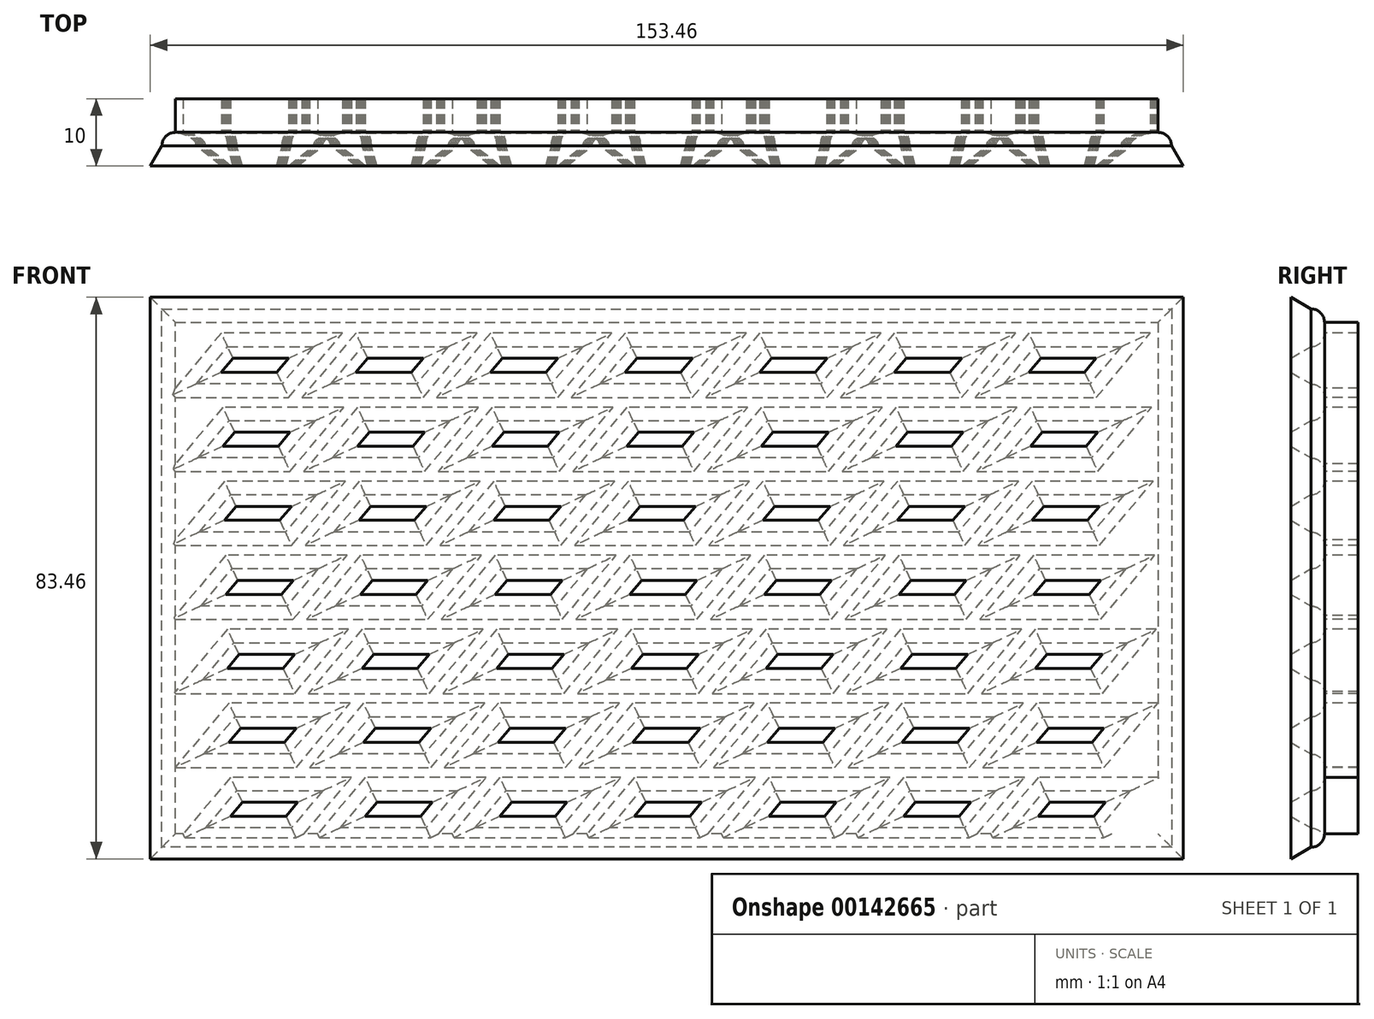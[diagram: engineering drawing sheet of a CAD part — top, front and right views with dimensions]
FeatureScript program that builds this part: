
annotation { "Feature Type Name" : "Feature", "Feature Type Description" : "" }
export const myFeature = defineFeature(function(context is Context, id is Id, definition is map)
    precondition{}
    {
        {
            var Q0;
            Q0=qCreatedBy(makeId("Front.planeOp"),FACE);
            var sketch = newSketch(context, id + "F0", { "sketchPlane" : qUnion([Q0])});
            skLineSegment(sketch, "E0", {"start": v(-73.34, 50) * mm, "end": v(76.66, 50) * mm});
            skLineSegment(sketch, "E1", {"start": v(76.66, 50) * mm, "end": v(76.66, -50) * mm});
            skLineSegment(sketch, "E2", {"start": v(76.66, -50) * mm, "end": v(-73.34, -50) * mm});
            skLineSegment(sketch, "E3", {"start": v(-73.34, -50) * mm, "end": v(-73.34, 50) * mm});
            skLineSegment(sketch, "E4", {"start": v(-73.34, 40) * mm, "end": v(76.66, 40) * mm});
            skLineSegment(sketch, "E5.0", {"start": v(76.66, -40) * mm, "end": v(-73.34, -40) * mm});
            skSolve(sketch);
        }
        {
            var Q0;
            Q0=qCreatedBy(makeId("Front.planeOp"),FACE);
            var sketch = newSketch(context, id + "F1", { "sketchPlane" : qUnion([Q0])});
            skLineSegment(sketch, "E6", {"start": v(-68.22, 28.84) * mm, "end": v(-55.46, 28.84) * mm});
            skLineSegment(sketch, "E7", {"start": v(-55.46, 28.84) * mm, "end": v(-50.8, 34.39) * mm});
            skLineSegment(sketch, "E8", {"start": v(-50.8, 34.39) * mm, "end": v(-63.57, 34.39) * mm});
            skLineSegment(sketch, "E9", {"start": v(-63.57, 34.39) * mm, "end": v(-68.22, 28.84) * mm});
            skLineSegment(sketch, "E10.0.1.0", {"start": v(-50.58, 23.39) * mm, "end": v(-63.34, 23.39) * mm});
            skLineSegment(sketch, "E10.0.1.1", {"start": v(-68, 17.84) * mm, "end": v(-55.24, 17.84) * mm});
            skLineSegment(sketch, "E10.0.1.2", {"start": v(-55.24, 17.84) * mm, "end": v(-50.58, 23.39) * mm});
            skLineSegment(sketch, "E10.0.1.3", {"start": v(-63.34, 23.39) * mm, "end": v(-68, 17.84) * mm});
            skLineSegment(sketch, "E10.0.2.0", {"start": v(-50.35, 12.4) * mm, "end": v(-63.11, 12.4) * mm});
            skLineSegment(sketch, "E10.0.2.1", {"start": v(-67.77, 6.84) * mm, "end": v(-55, 6.84) * mm});
            skLineSegment(sketch, "E10.0.2.2", {"start": v(-55, 6.84) * mm, "end": v(-50.35, 12.4) * mm});
            skLineSegment(sketch, "E10.0.2.3", {"start": v(-63.11, 12.4) * mm, "end": v(-67.77, 6.84) * mm});
            skLineSegment(sketch, "E10.0.3.0", {"start": v(-50.12, 1.4) * mm, "end": v(-62.88, 1.4) * mm});
            skLineSegment(sketch, "E10.0.3.1", {"start": v(-67.54, -4.15) * mm, "end": v(-54.78, -4.15) * mm});
            skLineSegment(sketch, "E10.0.3.2", {"start": v(-54.78, -4.15) * mm, "end": v(-50.12, 1.4) * mm});
            skLineSegment(sketch, "E10.0.3.3", {"start": v(-62.88, 1.4) * mm, "end": v(-67.54, -4.15) * mm});
            skLineSegment(sketch, "E10.0.4.0", {"start": v(-49.9, -9.6) * mm, "end": v(-62.66, -9.6) * mm});
            skLineSegment(sketch, "E10.0.4.1", {"start": v(-67.31, -15.15) * mm, "end": v(-54.55, -15.15) * mm});
            skLineSegment(sketch, "E10.0.4.2", {"start": v(-54.55, -15.15) * mm, "end": v(-49.9, -9.6) * mm});
            skLineSegment(sketch, "E10.0.4.3", {"start": v(-62.66, -9.6) * mm, "end": v(-67.31, -15.15) * mm});
            skLineSegment(sketch, "E10.0.5.0", {"start": v(-49.67, -20.6) * mm, "end": v(-62.43, -20.6) * mm});
            skLineSegment(sketch, "E10.0.5.1", {"start": v(-67.08, -26.15) * mm, "end": v(-54.32, -26.15) * mm});
            skLineSegment(sketch, "E10.0.5.2", {"start": v(-54.32, -26.15) * mm, "end": v(-49.67, -20.6) * mm});
            skLineSegment(sketch, "E10.0.5.3", {"start": v(-62.43, -20.6) * mm, "end": v(-67.08, -26.15) * mm});
            skLineSegment(sketch, "E10.0.6.0", {"start": v(-49.44, -31.6) * mm, "end": v(-62.2, -31.6) * mm});
            skLineSegment(sketch, "E10.0.6.1", {"start": v(-66.86, -37.15) * mm, "end": v(-54.1, -37.15) * mm});
            skLineSegment(sketch, "E10.0.6.2", {"start": v(-54.1, -37.15) * mm, "end": v(-49.44, -31.6) * mm});
            skLineSegment(sketch, "E10.0.6.3", {"start": v(-62.2, -31.6) * mm, "end": v(-66.86, -37.15) * mm});
            skLineSegment(sketch, "E10.1.0.0", {"start": v(-30.8, 34.39) * mm, "end": v(-43.57, 34.39) * mm});
            skLineSegment(sketch, "E10.1.0.1", {"start": v(-48.22, 28.84) * mm, "end": v(-35.46, 28.84) * mm});
            skLineSegment(sketch, "E10.1.0.2", {"start": v(-35.46, 28.84) * mm, "end": v(-30.8, 34.39) * mm});
            skLineSegment(sketch, "E10.1.0.3", {"start": v(-43.57, 34.39) * mm, "end": v(-48.22, 28.84) * mm});
            skLineSegment(sketch, "E10.1.1.0", {"start": v(-30.58, 23.39) * mm, "end": v(-43.34, 23.39) * mm});
            skLineSegment(sketch, "E10.1.1.1", {"start": v(-48, 17.84) * mm, "end": v(-35.24, 17.84) * mm});
            skLineSegment(sketch, "E10.1.1.2", {"start": v(-35.24, 17.84) * mm, "end": v(-30.58, 23.39) * mm});
            skLineSegment(sketch, "E10.1.1.3", {"start": v(-43.34, 23.39) * mm, "end": v(-48, 17.84) * mm});
            skLineSegment(sketch, "E10.1.2.0", {"start": v(-30.35, 12.4) * mm, "end": v(-43.11, 12.4) * mm});
            skLineSegment(sketch, "E10.1.2.1", {"start": v(-47.77, 6.84) * mm, "end": v(-35, 6.84) * mm});
            skLineSegment(sketch, "E10.1.2.2", {"start": v(-35, 6.84) * mm, "end": v(-30.35, 12.4) * mm});
            skLineSegment(sketch, "E10.1.2.3", {"start": v(-43.11, 12.4) * mm, "end": v(-47.77, 6.84) * mm});
            skLineSegment(sketch, "E10.1.3.0", {"start": v(-30.12, 1.4) * mm, "end": v(-42.88, 1.4) * mm});
            skLineSegment(sketch, "E10.1.3.1", {"start": v(-47.54, -4.15) * mm, "end": v(-34.78, -4.15) * mm});
            skLineSegment(sketch, "E10.1.3.2", {"start": v(-34.78, -4.15) * mm, "end": v(-30.12, 1.4) * mm});
            skLineSegment(sketch, "E10.1.3.3", {"start": v(-42.88, 1.4) * mm, "end": v(-47.54, -4.15) * mm});
            skLineSegment(sketch, "E10.1.4.0", {"start": v(-29.9, -9.6) * mm, "end": v(-42.66, -9.6) * mm});
            skLineSegment(sketch, "E10.1.4.1", {"start": v(-47.31, -15.15) * mm, "end": v(-34.55, -15.15) * mm});
            skLineSegment(sketch, "E10.1.4.2", {"start": v(-34.55, -15.15) * mm, "end": v(-29.9, -9.6) * mm});
            skLineSegment(sketch, "E10.1.4.3", {"start": v(-42.66, -9.6) * mm, "end": v(-47.31, -15.15) * mm});
            skLineSegment(sketch, "E10.1.5.0", {"start": v(-29.67, -20.6) * mm, "end": v(-42.43, -20.6) * mm});
            skLineSegment(sketch, "E10.1.5.1", {"start": v(-47.08, -26.15) * mm, "end": v(-34.32, -26.15) * mm});
            skLineSegment(sketch, "E10.1.5.2", {"start": v(-34.32, -26.15) * mm, "end": v(-29.67, -20.6) * mm});
            skLineSegment(sketch, "E10.1.5.3", {"start": v(-42.43, -20.6) * mm, "end": v(-47.08, -26.15) * mm});
            skLineSegment(sketch, "E10.1.6.0", {"start": v(-29.44, -31.6) * mm, "end": v(-42.2, -31.6) * mm});
            skLineSegment(sketch, "E10.1.6.1", {"start": v(-46.86, -37.15) * mm, "end": v(-34.1, -37.15) * mm});
            skLineSegment(sketch, "E10.1.6.2", {"start": v(-34.1, -37.15) * mm, "end": v(-29.44, -31.6) * mm});
            skLineSegment(sketch, "E10.1.6.3", {"start": v(-42.2, -31.6) * mm, "end": v(-46.86, -37.15) * mm});
            skLineSegment(sketch, "E10.2.0.0", {"start": v(-10.8, 34.39) * mm, "end": v(-23.57, 34.39) * mm});
            skLineSegment(sketch, "E10.2.0.1", {"start": v(-28.22, 28.84) * mm, "end": v(-15.46, 28.84) * mm});
            skLineSegment(sketch, "E10.2.0.2", {"start": v(-15.46, 28.84) * mm, "end": v(-10.8, 34.39) * mm});
            skLineSegment(sketch, "E10.2.0.3", {"start": v(-23.57, 34.39) * mm, "end": v(-28.22, 28.84) * mm});
            skLineSegment(sketch, "E10.2.1.0", {"start": v(-10.58, 23.39) * mm, "end": v(-23.34, 23.39) * mm});
            skLineSegment(sketch, "E10.2.1.1", {"start": v(-28, 17.84) * mm, "end": v(-15.24, 17.84) * mm});
            skLineSegment(sketch, "E10.2.1.2", {"start": v(-15.24, 17.84) * mm, "end": v(-10.58, 23.39) * mm});
            skLineSegment(sketch, "E10.2.1.3", {"start": v(-23.34, 23.39) * mm, "end": v(-28, 17.84) * mm});
            skLineSegment(sketch, "E10.2.2.0", {"start": v(-10.35, 12.4) * mm, "end": v(-23.11, 12.4) * mm});
            skLineSegment(sketch, "E10.2.2.1", {"start": v(-27.77, 6.84) * mm, "end": v(-15, 6.84) * mm});
            skLineSegment(sketch, "E10.2.2.2", {"start": v(-15, 6.84) * mm, "end": v(-10.35, 12.4) * mm});
            skLineSegment(sketch, "E10.2.2.3", {"start": v(-23.11, 12.4) * mm, "end": v(-27.77, 6.84) * mm});
            skLineSegment(sketch, "E10.2.3.0", {"start": v(-10.12, 1.4) * mm, "end": v(-22.88, 1.4) * mm});
            skLineSegment(sketch, "E10.2.3.1", {"start": v(-27.54, -4.15) * mm, "end": v(-14.78, -4.15) * mm});
            skLineSegment(sketch, "E10.2.3.2", {"start": v(-14.78, -4.15) * mm, "end": v(-10.12, 1.4) * mm});
            skLineSegment(sketch, "E10.2.3.3", {"start": v(-22.88, 1.4) * mm, "end": v(-27.54, -4.15) * mm});
            skLineSegment(sketch, "E10.2.4.0", {"start": v(-9.9, -9.6) * mm, "end": v(-22.66, -9.6) * mm});
            skLineSegment(sketch, "E10.2.4.1", {"start": v(-27.31, -15.15) * mm, "end": v(-14.55, -15.15) * mm});
            skLineSegment(sketch, "E10.2.4.2", {"start": v(-14.55, -15.15) * mm, "end": v(-9.9, -9.6) * mm});
            skLineSegment(sketch, "E10.2.4.3", {"start": v(-22.66, -9.6) * mm, "end": v(-27.31, -15.15) * mm});
            skLineSegment(sketch, "E10.2.5.0", {"start": v(-9.67, -20.6) * mm, "end": v(-22.43, -20.6) * mm});
            skLineSegment(sketch, "E10.2.5.1", {"start": v(-27.08, -26.15) * mm, "end": v(-14.32, -26.15) * mm});
            skLineSegment(sketch, "E10.2.5.2", {"start": v(-14.32, -26.15) * mm, "end": v(-9.67, -20.6) * mm});
            skLineSegment(sketch, "E10.2.5.3", {"start": v(-22.43, -20.6) * mm, "end": v(-27.08, -26.15) * mm});
            skLineSegment(sketch, "E10.2.6.0", {"start": v(-9.44, -31.6) * mm, "end": v(-22.2, -31.6) * mm});
            skLineSegment(sketch, "E10.2.6.1", {"start": v(-26.86, -37.15) * mm, "end": v(-14.1, -37.15) * mm});
            skLineSegment(sketch, "E10.2.6.2", {"start": v(-14.1, -37.15) * mm, "end": v(-9.44, -31.6) * mm});
            skLineSegment(sketch, "E10.2.6.3", {"start": v(-22.2, -31.6) * mm, "end": v(-26.86, -37.15) * mm});
            skLineSegment(sketch, "E10.3.0.0", {"start": v(9.2, 34.39) * mm, "end": v(-3.57, 34.39) * mm});
            skLineSegment(sketch, "E10.3.0.1", {"start": v(-8.22, 28.84) * mm, "end": v(4.54, 28.84) * mm});
            skLineSegment(sketch, "E10.3.0.2", {"start": v(4.54, 28.84) * mm, "end": v(9.2, 34.39) * mm});
            skLineSegment(sketch, "E10.3.0.3", {"start": v(-3.57, 34.39) * mm, "end": v(-8.22, 28.84) * mm});
            skLineSegment(sketch, "E10.3.1.0", {"start": v(9.42, 23.39) * mm, "end": v(-3.34, 23.39) * mm});
            skLineSegment(sketch, "E10.3.1.1", {"start": v(-8, 17.84) * mm, "end": v(4.76, 17.84) * mm});
            skLineSegment(sketch, "E10.3.1.2", {"start": v(4.76, 17.84) * mm, "end": v(9.42, 23.39) * mm});
            skLineSegment(sketch, "E10.3.1.3", {"start": v(-3.34, 23.39) * mm, "end": v(-8, 17.84) * mm});
            skLineSegment(sketch, "E10.3.2.0", {"start": v(9.65, 12.4) * mm, "end": v(-3.11, 12.4) * mm});
            skLineSegment(sketch, "E10.3.2.1", {"start": v(-7.77, 6.84) * mm, "end": v(5, 6.84) * mm});
            skLineSegment(sketch, "E10.3.2.2", {"start": v(5, 6.84) * mm, "end": v(9.65, 12.4) * mm});
            skLineSegment(sketch, "E10.3.2.3", {"start": v(-3.11, 12.4) * mm, "end": v(-7.77, 6.84) * mm});
            skLineSegment(sketch, "E10.3.3.0", {"start": v(9.88, 1.4) * mm, "end": v(-2.88, 1.4) * mm});
            skLineSegment(sketch, "E10.3.3.1", {"start": v(-7.54, -4.15) * mm, "end": v(5.22, -4.15) * mm});
            skLineSegment(sketch, "E10.3.3.2", {"start": v(5.22, -4.15) * mm, "end": v(9.88, 1.4) * mm});
            skLineSegment(sketch, "E10.3.3.3", {"start": v(-2.88, 1.4) * mm, "end": v(-7.54, -4.15) * mm});
            skLineSegment(sketch, "E10.3.4.0", {"start": v(10.1, -9.6) * mm, "end": v(-2.66, -9.6) * mm});
            skLineSegment(sketch, "E10.3.4.1", {"start": v(-7.31, -15.15) * mm, "end": v(5.45, -15.15) * mm});
            skLineSegment(sketch, "E10.3.4.2", {"start": v(5.45, -15.15) * mm, "end": v(10.1, -9.6) * mm});
            skLineSegment(sketch, "E10.3.4.3", {"start": v(-2.66, -9.6) * mm, "end": v(-7.31, -15.15) * mm});
            skLineSegment(sketch, "E10.3.5.0", {"start": v(10.33, -20.6) * mm, "end": v(-2.43, -20.6) * mm});
            skLineSegment(sketch, "E10.3.5.1", {"start": v(-7.08, -26.15) * mm, "end": v(5.68, -26.15) * mm});
            skLineSegment(sketch, "E10.3.5.2", {"start": v(5.68, -26.15) * mm, "end": v(10.33, -20.6) * mm});
            skLineSegment(sketch, "E10.3.5.3", {"start": v(-2.43, -20.6) * mm, "end": v(-7.08, -26.15) * mm});
            skLineSegment(sketch, "E10.3.6.0", {"start": v(10.56, -31.6) * mm, "end": v(-2.2, -31.6) * mm});
            skLineSegment(sketch, "E10.3.6.1", {"start": v(-6.86, -37.15) * mm, "end": v(5.9, -37.15) * mm});
            skLineSegment(sketch, "E10.3.6.2", {"start": v(5.9, -37.15) * mm, "end": v(10.56, -31.6) * mm});
            skLineSegment(sketch, "E10.3.6.3", {"start": v(-2.2, -31.6) * mm, "end": v(-6.86, -37.15) * mm});
            skLineSegment(sketch, "E10.4.0.0", {"start": v(29.2, 34.39) * mm, "end": v(16.43, 34.39) * mm});
            skLineSegment(sketch, "E10.4.0.1", {"start": v(11.78, 28.84) * mm, "end": v(24.54, 28.84) * mm});
            skLineSegment(sketch, "E10.4.0.2", {"start": v(24.54, 28.84) * mm, "end": v(29.2, 34.39) * mm});
            skLineSegment(sketch, "E10.4.0.3", {"start": v(16.43, 34.39) * mm, "end": v(11.78, 28.84) * mm});
            skLineSegment(sketch, "E10.4.1.0", {"start": v(29.42, 23.39) * mm, "end": v(16.66, 23.39) * mm});
            skLineSegment(sketch, "E10.4.1.1", {"start": v(12, 17.84) * mm, "end": v(24.76, 17.84) * mm});
            skLineSegment(sketch, "E10.4.1.2", {"start": v(24.76, 17.84) * mm, "end": v(29.42, 23.39) * mm});
            skLineSegment(sketch, "E10.4.1.3", {"start": v(16.66, 23.39) * mm, "end": v(12, 17.84) * mm});
            skLineSegment(sketch, "E10.4.2.0", {"start": v(29.65, 12.4) * mm, "end": v(16.89, 12.4) * mm});
            skLineSegment(sketch, "E10.4.2.1", {"start": v(12.23, 6.84) * mm, "end": v(25, 6.84) * mm});
            skLineSegment(sketch, "E10.4.2.2", {"start": v(25, 6.84) * mm, "end": v(29.65, 12.4) * mm});
            skLineSegment(sketch, "E10.4.2.3", {"start": v(16.89, 12.4) * mm, "end": v(12.23, 6.84) * mm});
            skLineSegment(sketch, "E10.4.3.0", {"start": v(29.88, 1.4) * mm, "end": v(17.12, 1.4) * mm});
            skLineSegment(sketch, "E10.4.3.1", {"start": v(12.46, -4.15) * mm, "end": v(25.22, -4.15) * mm});
            skLineSegment(sketch, "E10.4.3.2", {"start": v(25.22, -4.15) * mm, "end": v(29.88, 1.4) * mm});
            skLineSegment(sketch, "E10.4.3.3", {"start": v(17.12, 1.4) * mm, "end": v(12.46, -4.15) * mm});
            skLineSegment(sketch, "E10.4.4.0", {"start": v(30.1, -9.6) * mm, "end": v(17.34, -9.6) * mm});
            skLineSegment(sketch, "E10.4.4.1", {"start": v(12.69, -15.15) * mm, "end": v(25.45, -15.15) * mm});
            skLineSegment(sketch, "E10.4.4.2", {"start": v(25.45, -15.15) * mm, "end": v(30.1, -9.6) * mm});
            skLineSegment(sketch, "E10.4.4.3", {"start": v(17.34, -9.6) * mm, "end": v(12.69, -15.15) * mm});
            skLineSegment(sketch, "E10.4.5.0", {"start": v(30.33, -20.6) * mm, "end": v(17.57, -20.6) * mm});
            skLineSegment(sketch, "E10.4.5.1", {"start": v(12.92, -26.15) * mm, "end": v(25.68, -26.15) * mm});
            skLineSegment(sketch, "E10.4.5.2", {"start": v(25.68, -26.15) * mm, "end": v(30.33, -20.6) * mm});
            skLineSegment(sketch, "E10.4.5.3", {"start": v(17.57, -20.6) * mm, "end": v(12.92, -26.15) * mm});
            skLineSegment(sketch, "E10.4.6.0", {"start": v(30.56, -31.6) * mm, "end": v(17.8, -31.6) * mm});
            skLineSegment(sketch, "E10.4.6.1", {"start": v(13.14, -37.15) * mm, "end": v(25.9, -37.15) * mm});
            skLineSegment(sketch, "E10.4.6.2", {"start": v(25.9, -37.15) * mm, "end": v(30.56, -31.6) * mm});
            skLineSegment(sketch, "E10.4.6.3", {"start": v(17.8, -31.6) * mm, "end": v(13.14, -37.15) * mm});
            skLineSegment(sketch, "E10.5.0.0", {"start": v(49.2, 34.39) * mm, "end": v(36.43, 34.39) * mm});
            skLineSegment(sketch, "E10.5.0.1", {"start": v(31.78, 28.84) * mm, "end": v(44.54, 28.84) * mm});
            skLineSegment(sketch, "E10.5.0.2", {"start": v(44.54, 28.84) * mm, "end": v(49.2, 34.39) * mm});
            skLineSegment(sketch, "E10.5.0.3", {"start": v(36.43, 34.39) * mm, "end": v(31.78, 28.84) * mm});
            skLineSegment(sketch, "E10.5.1.0", {"start": v(49.42, 23.39) * mm, "end": v(36.66, 23.39) * mm});
            skLineSegment(sketch, "E10.5.1.1", {"start": v(32, 17.84) * mm, "end": v(44.76, 17.84) * mm});
            skLineSegment(sketch, "E10.5.1.2", {"start": v(44.76, 17.84) * mm, "end": v(49.42, 23.39) * mm});
            skLineSegment(sketch, "E10.5.1.3", {"start": v(36.66, 23.39) * mm, "end": v(32, 17.84) * mm});
            skLineSegment(sketch, "E10.5.2.0", {"start": v(49.65, 12.4) * mm, "end": v(36.89, 12.4) * mm});
            skLineSegment(sketch, "E10.5.2.1", {"start": v(32.23, 6.84) * mm, "end": v(45, 6.84) * mm});
            skLineSegment(sketch, "E10.5.2.2", {"start": v(45, 6.84) * mm, "end": v(49.65, 12.4) * mm});
            skLineSegment(sketch, "E10.5.2.3", {"start": v(36.89, 12.4) * mm, "end": v(32.23, 6.84) * mm});
            skLineSegment(sketch, "E10.5.3.0", {"start": v(49.88, 1.4) * mm, "end": v(37.12, 1.4) * mm});
            skLineSegment(sketch, "E10.5.3.1", {"start": v(32.46, -4.15) * mm, "end": v(45.22, -4.15) * mm});
            skLineSegment(sketch, "E10.5.3.2", {"start": v(45.22, -4.15) * mm, "end": v(49.88, 1.4) * mm});
            skLineSegment(sketch, "E10.5.3.3", {"start": v(37.12, 1.4) * mm, "end": v(32.46, -4.15) * mm});
            skLineSegment(sketch, "E10.5.4.0", {"start": v(50.1, -9.6) * mm, "end": v(37.34, -9.6) * mm});
            skLineSegment(sketch, "E10.5.4.1", {"start": v(32.69, -15.15) * mm, "end": v(45.45, -15.15) * mm});
            skLineSegment(sketch, "E10.5.4.2", {"start": v(45.45, -15.15) * mm, "end": v(50.1, -9.6) * mm});
            skLineSegment(sketch, "E10.5.4.3", {"start": v(37.34, -9.6) * mm, "end": v(32.69, -15.15) * mm});
            skLineSegment(sketch, "E10.5.5.0", {"start": v(50.33, -20.6) * mm, "end": v(37.57, -20.6) * mm});
            skLineSegment(sketch, "E10.5.5.1", {"start": v(32.92, -26.15) * mm, "end": v(45.68, -26.15) * mm});
            skLineSegment(sketch, "E10.5.5.2", {"start": v(45.68, -26.15) * mm, "end": v(50.33, -20.6) * mm});
            skLineSegment(sketch, "E10.5.5.3", {"start": v(37.57, -20.6) * mm, "end": v(32.92, -26.15) * mm});
            skLineSegment(sketch, "E10.5.6.0", {"start": v(50.56, -31.6) * mm, "end": v(37.8, -31.6) * mm});
            skLineSegment(sketch, "E10.5.6.1", {"start": v(33.14, -37.15) * mm, "end": v(45.9, -37.15) * mm});
            skLineSegment(sketch, "E10.5.6.2", {"start": v(45.9, -37.15) * mm, "end": v(50.56, -31.6) * mm});
            skLineSegment(sketch, "E10.5.6.3", {"start": v(37.8, -31.6) * mm, "end": v(33.14, -37.15) * mm});
            skLineSegment(sketch, "E10.6.0.0", {"start": v(69.2, 34.39) * mm, "end": v(56.43, 34.39) * mm});
            skLineSegment(sketch, "E10.6.0.1", {"start": v(51.78, 28.84) * mm, "end": v(64.54, 28.84) * mm});
            skLineSegment(sketch, "E10.6.0.2", {"start": v(64.54, 28.84) * mm, "end": v(69.2, 34.39) * mm});
            skLineSegment(sketch, "E10.6.0.3", {"start": v(56.43, 34.39) * mm, "end": v(51.78, 28.84) * mm});
            skLineSegment(sketch, "E10.6.1.0", {"start": v(69.42, 23.39) * mm, "end": v(56.66, 23.39) * mm});
            skLineSegment(sketch, "E10.6.1.1", {"start": v(52, 17.84) * mm, "end": v(64.76, 17.84) * mm});
            skLineSegment(sketch, "E10.6.1.2", {"start": v(64.76, 17.84) * mm, "end": v(69.42, 23.39) * mm});
            skLineSegment(sketch, "E10.6.1.3", {"start": v(56.66, 23.39) * mm, "end": v(52, 17.84) * mm});
            skLineSegment(sketch, "E10.6.2.0", {"start": v(69.65, 12.4) * mm, "end": v(56.89, 12.4) * mm});
            skLineSegment(sketch, "E10.6.2.1", {"start": v(52.23, 6.84) * mm, "end": v(65, 6.84) * mm});
            skLineSegment(sketch, "E10.6.2.2", {"start": v(65, 6.84) * mm, "end": v(69.65, 12.4) * mm});
            skLineSegment(sketch, "E10.6.2.3", {"start": v(56.89, 12.4) * mm, "end": v(52.23, 6.84) * mm});
            skLineSegment(sketch, "E10.6.3.0", {"start": v(69.88, 1.4) * mm, "end": v(57.12, 1.4) * mm});
            skLineSegment(sketch, "E10.6.3.1", {"start": v(52.46, -4.15) * mm, "end": v(65.22, -4.15) * mm});
            skLineSegment(sketch, "E10.6.3.2", {"start": v(65.22, -4.15) * mm, "end": v(69.88, 1.4) * mm});
            skLineSegment(sketch, "E10.6.3.3", {"start": v(57.12, 1.4) * mm, "end": v(52.46, -4.15) * mm});
            skLineSegment(sketch, "E10.6.4.0", {"start": v(70.1, -9.6) * mm, "end": v(57.34, -9.6) * mm});
            skLineSegment(sketch, "E10.6.4.1", {"start": v(52.69, -15.15) * mm, "end": v(65.45, -15.15) * mm});
            skLineSegment(sketch, "E10.6.4.2", {"start": v(65.45, -15.15) * mm, "end": v(70.1, -9.6) * mm});
            skLineSegment(sketch, "E10.6.4.3", {"start": v(57.34, -9.6) * mm, "end": v(52.69, -15.15) * mm});
            skLineSegment(sketch, "E10.6.5.0", {"start": v(70.33, -20.6) * mm, "end": v(57.57, -20.6) * mm});
            skLineSegment(sketch, "E10.6.5.1", {"start": v(52.92, -26.15) * mm, "end": v(65.68, -26.15) * mm});
            skLineSegment(sketch, "E10.6.5.2", {"start": v(65.68, -26.15) * mm, "end": v(70.33, -20.6) * mm});
            skLineSegment(sketch, "E10.6.5.3", {"start": v(57.57, -20.6) * mm, "end": v(52.92, -26.15) * mm});
            skLineSegment(sketch, "E10.6.6.0", {"start": v(70.56, -31.6) * mm, "end": v(57.8, -31.6) * mm});
            skLineSegment(sketch, "E10.6.6.1", {"start": v(53.14, -37.15) * mm, "end": v(65.9, -37.15) * mm});
            skLineSegment(sketch, "E10.6.6.2", {"start": v(65.9, -37.15) * mm, "end": v(70.56, -31.6) * mm});
            skLineSegment(sketch, "E10.6.6.3", {"start": v(57.8, -31.6) * mm, "end": v(53.14, -37.15) * mm});
            skLineSegment(sketch, "E10.direction1", {"start": v(-55.46, 28.84) * mm, "end": v(-35.46, 28.84) * mm, "construction": true});
            skLineSegment(sketch, "E10.direction2", {"start": v(-55.46, 28.84) * mm, "end": v(-55.24, 17.84) * mm, "construction": true});
            skSolve(sketch);
        }
        {
            var Q0;
            {var subQ0=sQuery(id+"F0.wireOp",EDGE,"E4");Q0=makeQuery(id+"F0.imprint","IMPRINT",FACE,{"disambiguationData":[TD([[makeQuery(id+"F0.imprint","IMPRINT",EDGE,{"derivedFrom":subQ0}),-1.0]])]});}
            extrude(context, id + "F6", {"entities" : qUnion([Q0]), "depth" : 2 * mm});
        }
        {
            var Q0;
            Q0=makeQuery(id+"F1.imprint","IMPRINT",FACE,{"disambiguationData":[TD([[makeQuery(id+"F1.imprint","IMPRINT",EDGE,{"derivedFrom":sQuery(id+"F1.wireOp",EDGE,"E10.6.6.0")}),1.0]])]});
            var Q1;
            Q1=makeQuery(id+"F1.imprint","IMPRINT",FACE,{"disambiguationData":[TD([[makeQuery(id+"F1.imprint","IMPRINT",EDGE,{"derivedFrom":sQuery(id+"F1.wireOp",EDGE,"E10.6.5.0")}),1.0]])]});
            var Q2;
            Q2=makeQuery(id+"F1.imprint","IMPRINT",FACE,{"disambiguationData":[TD([[makeQuery(id+"F1.imprint","IMPRINT",EDGE,{"derivedFrom":sQuery(id+"F1.wireOp",EDGE,"E10.6.4.0")}),1.0]])]});
            var Q3;
            Q3=makeQuery(id+"F1.imprint","IMPRINT",FACE,{"disambiguationData":[TD([[makeQuery(id+"F1.imprint","IMPRINT",EDGE,{"derivedFrom":sQuery(id+"F1.wireOp",EDGE,"E10.5.4.0")}),1.0]])]});
            var Q4;
            Q4=makeQuery(id+"F1.imprint","IMPRINT",FACE,{"disambiguationData":[TD([[makeQuery(id+"F1.imprint","IMPRINT",EDGE,{"derivedFrom":sQuery(id+"F1.wireOp",EDGE,"E10.5.5.0")}),1.0]])]});
            var Q5;
            Q5=makeQuery(id+"F1.imprint","IMPRINT",FACE,{"disambiguationData":[TD([[makeQuery(id+"F1.imprint","IMPRINT",EDGE,{"derivedFrom":sQuery(id+"F1.wireOp",EDGE,"E10.5.6.0")}),1.0]])]});
            var Q6;
            Q6=makeQuery(id+"F1.imprint","IMPRINT",FACE,{"disambiguationData":[TD([[makeQuery(id+"F1.imprint","IMPRINT",EDGE,{"derivedFrom":sQuery(id+"F1.wireOp",EDGE,"E10.4.6.0")}),1.0]])]});
            var Q7;
            Q7=makeQuery(id+"F1.imprint","IMPRINT",FACE,{"disambiguationData":[TD([[makeQuery(id+"F1.imprint","IMPRINT",EDGE,{"derivedFrom":sQuery(id+"F1.wireOp",EDGE,"E10.4.5.0")}),1.0]])]});
            var Q8;
            Q8=makeQuery(id+"F1.imprint","IMPRINT",FACE,{"disambiguationData":[TD([[makeQuery(id+"F1.imprint","IMPRINT",EDGE,{"derivedFrom":sQuery(id+"F1.wireOp",EDGE,"E10.4.4.0")}),1.0]])]});
            var Q9;
            Q9=makeQuery(id+"F1.imprint","IMPRINT",FACE,{"disambiguationData":[TD([[makeQuery(id+"F1.imprint","IMPRINT",EDGE,{"derivedFrom":sQuery(id+"F1.wireOp",EDGE,"E10.4.3.0")}),1.0]])]});
            var Q10;
            Q10=makeQuery(id+"F1.imprint","IMPRINT",FACE,{"disambiguationData":[TD([[makeQuery(id+"F1.imprint","IMPRINT",EDGE,{"derivedFrom":sQuery(id+"F1.wireOp",EDGE,"E10.5.3.0")}),1.0]])]});
            var Q11;
            Q11=makeQuery(id+"F1.imprint","IMPRINT",FACE,{"disambiguationData":[TD([[makeQuery(id+"F1.imprint","IMPRINT",EDGE,{"derivedFrom":sQuery(id+"F1.wireOp",EDGE,"E10.6.3.0")}),1.0]])]});
            var Q12;
            Q12=makeQuery(id+"F1.imprint","IMPRINT",FACE,{"disambiguationData":[TD([[makeQuery(id+"F1.imprint","IMPRINT",EDGE,{"derivedFrom":sQuery(id+"F1.wireOp",EDGE,"E10.6.2.0")}),1.0]])]});
            var Q13;
            Q13=makeQuery(id+"F1.imprint","IMPRINT",FACE,{"disambiguationData":[TD([[makeQuery(id+"F1.imprint","IMPRINT",EDGE,{"derivedFrom":sQuery(id+"F1.wireOp",EDGE,"E10.5.2.0")}),1.0]])]});
            var Q14;
            Q14=makeQuery(id+"F1.imprint","IMPRINT",FACE,{"disambiguationData":[TD([[makeQuery(id+"F1.imprint","IMPRINT",EDGE,{"derivedFrom":sQuery(id+"F1.wireOp",EDGE,"E10.4.2.0")}),1.0]])]});
            var Q15;
            Q15=makeQuery(id+"F1.imprint","IMPRINT",FACE,{"disambiguationData":[TD([[makeQuery(id+"F1.imprint","IMPRINT",EDGE,{"derivedFrom":sQuery(id+"F1.wireOp",EDGE,"E10.4.1.0")}),1.0]])]});
            var Q16;
            Q16=makeQuery(id+"F1.imprint","IMPRINT",FACE,{"disambiguationData":[TD([[makeQuery(id+"F1.imprint","IMPRINT",EDGE,{"derivedFrom":sQuery(id+"F1.wireOp",EDGE,"E10.4.0.0")}),1.0]])]});
            var Q17;
            Q17=makeQuery(id+"F1.imprint","IMPRINT",FACE,{"disambiguationData":[TD([[makeQuery(id+"F1.imprint","IMPRINT",EDGE,{"derivedFrom":sQuery(id+"F1.wireOp",EDGE,"E10.5.0.0")}),1.0]])]});
            var Q18;
            Q18=makeQuery(id+"F1.imprint","IMPRINT",FACE,{"disambiguationData":[TD([[makeQuery(id+"F1.imprint","IMPRINT",EDGE,{"derivedFrom":sQuery(id+"F1.wireOp",EDGE,"E10.5.1.0")}),1.0]])]});
            var Q19;
            Q19=makeQuery(id+"F1.imprint","IMPRINT",FACE,{"disambiguationData":[TD([[makeQuery(id+"F1.imprint","IMPRINT",EDGE,{"derivedFrom":sQuery(id+"F1.wireOp",EDGE,"E10.6.1.0")}),1.0]])]});
            var Q20;
            Q20=makeQuery(id+"F1.imprint","IMPRINT",FACE,{"disambiguationData":[TD([[makeQuery(id+"F1.imprint","IMPRINT",EDGE,{"derivedFrom":sQuery(id+"F1.wireOp",EDGE,"E10.6.0.0")}),1.0]])]});
            var Q21;
            Q21=makeQuery(id+"F1.imprint","IMPRINT",FACE,{"disambiguationData":[TD([[makeQuery(id+"F1.imprint","IMPRINT",EDGE,{"derivedFrom":sQuery(id+"F1.wireOp",EDGE,"E10.3.0.0")}),1.0]])]});
            var Q22;
            Q22=makeQuery(id+"F1.imprint","IMPRINT",FACE,{"disambiguationData":[TD([[makeQuery(id+"F1.imprint","IMPRINT",EDGE,{"derivedFrom":sQuery(id+"F1.wireOp",EDGE,"E10.2.0.0")}),1.0]])]});
            var Q23;
            Q23=makeQuery(id+"F1.imprint","IMPRINT",FACE,{"disambiguationData":[TD([[makeQuery(id+"F1.imprint","IMPRINT",EDGE,{"derivedFrom":sQuery(id+"F1.wireOp",EDGE,"E10.1.0.0")}),1.0]])]});
            var Q24;
            Q24=makeQuery(id+"F1.imprint","IMPRINT",FACE,{"disambiguationData":[TD([[makeQuery(id+"F1.imprint","IMPRINT",EDGE,{"derivedFrom":sQuery(id+"F1.wireOp",EDGE,"E10.1.1.0")}),1.0]])]});
            var Q25;
            Q25=makeQuery(id+"F1.imprint","IMPRINT",FACE,{"disambiguationData":[TD([[makeQuery(id+"F1.imprint","IMPRINT",EDGE,{"derivedFrom":sQuery(id+"F1.wireOp",EDGE,"E10.2.1.0")}),1.0]])]});
            var Q26;
            Q26=makeQuery(id+"F1.imprint","IMPRINT",FACE,{"disambiguationData":[TD([[makeQuery(id+"F1.imprint","IMPRINT",EDGE,{"derivedFrom":sQuery(id+"F1.wireOp",EDGE,"E10.3.1.0")}),1.0]])]});
            var Q27;
            Q27=makeQuery(id+"F1.imprint","IMPRINT",FACE,{"disambiguationData":[TD([[makeQuery(id+"F1.imprint","IMPRINT",EDGE,{"derivedFrom":sQuery(id+"F1.wireOp",EDGE,"E10.3.2.0")}),1.0]])]});
            var Q28;
            Q28=makeQuery(id+"F1.imprint","IMPRINT",FACE,{"disambiguationData":[TD([[makeQuery(id+"F1.imprint","IMPRINT",EDGE,{"derivedFrom":sQuery(id+"F1.wireOp",EDGE,"E10.3.3.0")}),1.0]])]});
            var Q29;
            Q29=makeQuery(id+"F1.imprint","IMPRINT",FACE,{"disambiguationData":[TD([[makeQuery(id+"F1.imprint","IMPRINT",EDGE,{"derivedFrom":sQuery(id+"F1.wireOp",EDGE,"E10.3.4.0")}),1.0]])]});
            var Q30;
            Q30=makeQuery(id+"F1.imprint","IMPRINT",FACE,{"disambiguationData":[TD([[makeQuery(id+"F1.imprint","IMPRINT",EDGE,{"derivedFrom":sQuery(id+"F1.wireOp",EDGE,"E10.3.5.0")}),1.0]])]});
            var Q31;
            Q31=makeQuery(id+"F1.imprint","IMPRINT",FACE,{"disambiguationData":[TD([[makeQuery(id+"F1.imprint","IMPRINT",EDGE,{"derivedFrom":sQuery(id+"F1.wireOp",EDGE,"E10.2.5.0")}),1.0]])]});
            var Q32;
            Q32=makeQuery(id+"F1.imprint","IMPRINT",FACE,{"disambiguationData":[TD([[makeQuery(id+"F1.imprint","IMPRINT",EDGE,{"derivedFrom":sQuery(id+"F1.wireOp",EDGE,"E10.2.4.0")}),1.0]])]});
            var Q33;
            Q33=makeQuery(id+"F1.imprint","IMPRINT",FACE,{"disambiguationData":[TD([[makeQuery(id+"F1.imprint","IMPRINT",EDGE,{"derivedFrom":sQuery(id+"F1.wireOp",EDGE,"E10.2.3.0")}),1.0]])]});
            var Q34;
            Q34=makeQuery(id+"F1.imprint","IMPRINT",FACE,{"disambiguationData":[TD([[makeQuery(id+"F1.imprint","IMPRINT",EDGE,{"derivedFrom":sQuery(id+"F1.wireOp",EDGE,"E10.2.2.0")}),1.0]])]});
            var Q35;
            Q35=makeQuery(id+"F1.imprint","IMPRINT",FACE,{"disambiguationData":[TD([[makeQuery(id+"F1.imprint","IMPRINT",EDGE,{"derivedFrom":sQuery(id+"F1.wireOp",EDGE,"E10.1.2.0")}),1.0]])]});
            var Q36;
            Q36=makeQuery(id+"F1.imprint","IMPRINT",FACE,{"disambiguationData":[TD([[makeQuery(id+"F1.imprint","IMPRINT",EDGE,{"derivedFrom":sQuery(id+"F1.wireOp",EDGE,"E10.1.3.0")}),1.0]])]});
            var Q37;
            Q37=makeQuery(id+"F1.imprint","IMPRINT",FACE,{"disambiguationData":[TD([[makeQuery(id+"F1.imprint","IMPRINT",EDGE,{"derivedFrom":sQuery(id+"F1.wireOp",EDGE,"E10.1.4.0")}),1.0]])]});
            var Q38;
            Q38=makeQuery(id+"F1.imprint","IMPRINT",FACE,{"disambiguationData":[TD([[makeQuery(id+"F1.imprint","IMPRINT",EDGE,{"derivedFrom":sQuery(id+"F1.wireOp",EDGE,"E10.3.6.0")}),1.0]])]});
            var Q39;
            Q39=makeQuery(id+"F1.imprint","IMPRINT",FACE,{"disambiguationData":[TD([[makeQuery(id+"F1.imprint","IMPRINT",EDGE,{"derivedFrom":sQuery(id+"F1.wireOp",EDGE,"E10.2.6.0")}),1.0]])]});
            var Q40;
            Q40=makeQuery(id+"F1.imprint","IMPRINT",FACE,{"disambiguationData":[TD([[makeQuery(id+"F1.imprint","IMPRINT",EDGE,{"derivedFrom":sQuery(id+"F1.wireOp",EDGE,"E10.1.6.0")}),1.0]])]});
            var Q41;
            Q41=makeQuery(id+"F1.imprint","IMPRINT",FACE,{"disambiguationData":[TD([[makeQuery(id+"F1.imprint","IMPRINT",EDGE,{"derivedFrom":sQuery(id+"F1.wireOp",EDGE,"E10.1.5.0")}),1.0]])]});
            var Q42;
            Q42=makeQuery(id+"F1.imprint","IMPRINT",FACE,{"disambiguationData":[TD([[makeQuery(id+"F1.imprint","IMPRINT",EDGE,{"derivedFrom":sQuery(id+"F1.wireOp",EDGE,"E10.0.6.0")}),1.0]])]});
            var Q43;
            Q43=makeQuery(id+"F1.imprint","IMPRINT",FACE,{"disambiguationData":[TD([[makeQuery(id+"F1.imprint","IMPRINT",EDGE,{"derivedFrom":sQuery(id+"F1.wireOp",EDGE,"E10.0.5.0")}),1.0]])]});
            var Q44;
            Q44=makeQuery(id+"F1.imprint","IMPRINT",FACE,{"disambiguationData":[TD([[makeQuery(id+"F1.imprint","IMPRINT",EDGE,{"derivedFrom":sQuery(id+"F1.wireOp",EDGE,"E10.0.4.0")}),1.0]])]});
            var Q45;
            Q45=makeQuery(id+"F1.imprint","IMPRINT",FACE,{"disambiguationData":[TD([[makeQuery(id+"F1.imprint","IMPRINT",EDGE,{"derivedFrom":sQuery(id+"F1.wireOp",EDGE,"E10.0.3.0")}),1.0]])]});
            var Q46;
            Q46=makeQuery(id+"F1.imprint","IMPRINT",FACE,{"disambiguationData":[TD([[makeQuery(id+"F1.imprint","IMPRINT",EDGE,{"derivedFrom":sQuery(id+"F1.wireOp",EDGE,"E10.0.2.0")}),1.0]])]});
            var Q47;
            Q47=makeQuery(id+"F1.imprint","IMPRINT",FACE,{"disambiguationData":[TD([[makeQuery(id+"F1.imprint","IMPRINT",EDGE,{"derivedFrom":sQuery(id+"F1.wireOp",EDGE,"E10.0.1.0")}),1.0]])]});
            var Q48;
            Q48=makeQuery(id+"F1.imprint","IMPRINT",FACE,{"disambiguationData":[TD([[makeQuery(id+"F1.imprint","IMPRINT",EDGE,{"derivedFrom":sQuery(id+"F1.wireOp",EDGE,"E6")}),1.0]])]});
            extrude(context, id + "F2", {"entities" : qUnion([Q0, Q1, Q2, Q3, Q4, Q5, Q6, Q7, Q8, Q9, Q10, Q11, Q12, Q13, Q14, Q15, Q16, Q17, Q18, Q19, Q20, Q21, Q22, Q23, Q24, Q25, Q26, Q27, Q28, Q29, Q30, Q31, Q32, Q33, Q34, Q35, Q36, Q37, Q38, Q39, Q40, Q41, Q42, Q43, Q44, Q45, Q46, Q47, Q48]), "operationType" : NewBodyOperationType.REMOVE, "depth" : 40.7 * mm});
        }
        {
            var Q0;
            Q0=makeQuery(id+"F6.opExtrude","CAP_FACE",FACE,{"disambiguationData":[OSD([sQuery(id+"F0.wireOp",EDGE,"E1"),sQuery(id+"F0.wireOp",EDGE,"E3"),sQuery(id+"F0.wireOp",EDGE,"E4"),sQuery(id+"F0.wireOp",EDGE,"E5.0")])],"isStart":false});
            extrude(context, id + "F3", {"entities" : qUnion([Q0]), "operationType" : NewBodyOperationType.ADD, "depth" : 3 * mm, "hasDraft" : true, "draftAngle" : 30 * degree});
        }
        {
            var Q0;
            Q0=makeQuery(id+"F6.opExtrude","CAP_FACE",FACE,{"disambiguationData":[OSD([sQuery(id+"F0.wireOp",EDGE,"E1"),sQuery(id+"F0.wireOp",EDGE,"E3"),sQuery(id+"F0.wireOp",EDGE,"E4"),sQuery(id+"F0.wireOp",EDGE,"E5.0")])],"isStart":true});
            fillet(context, id + "F4", {"entities" : qUnion([Q0]), "radius" : 2 * mm, "tangentPropagation" : true, "allowEdgeOverflow" : false});
        }
        {
            var Q0;
            Q0=makeQuery(id+"F4.opFillet","SPLIT",FACE,{"disambiguationData":[OD(1.0)],"derivedFrom":makeQuery(id+"F6.opExtrude","CAP_FACE",FACE,{"disambiguationData":[OSD([sQuery(id+"F0.wireOp",EDGE,"E1"),sQuery(id+"F0.wireOp",EDGE,"E3"),sQuery(id+"F0.wireOp",EDGE,"E4"),sQuery(id+"F0.wireOp",EDGE,"E5.0")])],"isStart":true})});
            extrude(context, id + "F5", {"entities" : qUnion([Q0]), "operationType" : NewBodyOperationType.ADD, "depth" : 5 * mm});
        }
    });
